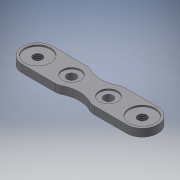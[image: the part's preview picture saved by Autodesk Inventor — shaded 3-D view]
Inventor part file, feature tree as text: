
AUTODESK INVENTOR PART (.ipt)
format: ipt  version: 2019.4 (Build 234330000, 330)  size: 178,688 bytes
history: native  units: mm
features: sketch x7, extrude x6, mirror x2, hole x1, fillet x1
ambient origin geometry x8: Origin, YZ Plane, XZ Plane, XY Plane, X Axis, Y Axis, Z Axis, Center Point
bodies: Solid1 (feature_tree)
feature tree (17):
  extrude  "Extrusion1"  Depth=10.0mm
  extrude  "Extrusion2"  Depth=2.5mm TaperAngle=0.0deg
  hole  "Hole1"  [1 undecoded]
  extrude  "Extrusion3"  Depth=2.0mm
  extrude  "Extrusion4"  Depth=0.5mm TaperAngle=0.0deg
  mirror  "Mirror1"
  extrude  "Extrusion5"  Depth=5.0mm
  extrude  "Extrusion6"  Depth=5.0mm
  mirror  "Mirror2"
  fillet  "Fillet1"  Radius=20.0mm
  sketch  "Sketch1"  dims[d0=34.0mm d1=10.0mm]
  sketch  "Sketch2"  dims[d2=2.5mm d3=0.0mm d4=2.5mm d5=0.0mm]
  sketch  "Sketch3"  dims[d6=3.0mm d7=3.0mm]
  sketch  "Sketch4"  dims[d8=2.85mm d9=7.0mm d10=6.0mm d11=2.0mm d12=90.0deg d13=8.0mm d14=20.594885mm d15=8.5mm]
  sketch  "Sketch5"  dims[d16=8.5mm d17=0.5mm d18=0.0mm]
  sketch  "Sketch6"  dims[d19=3.0mm d20=5.0mm]
  sketch  "Sketch7"  dims[d21=3.0mm d22=5.0mm d23=20.0mm d24=0.5mm d25=0.0mm d26=6.0mm d27=6.0mm d28=0.5mm d29=0.0mm d30=3.0mm d31=0.5mm d32=0.0mm d33=4.0mm]
note: 1 required parameter value undecoded (feature->parameter linkage not recoverable at this tier; creation-order binding heuristic only, values carry confidence <= 0.55)
